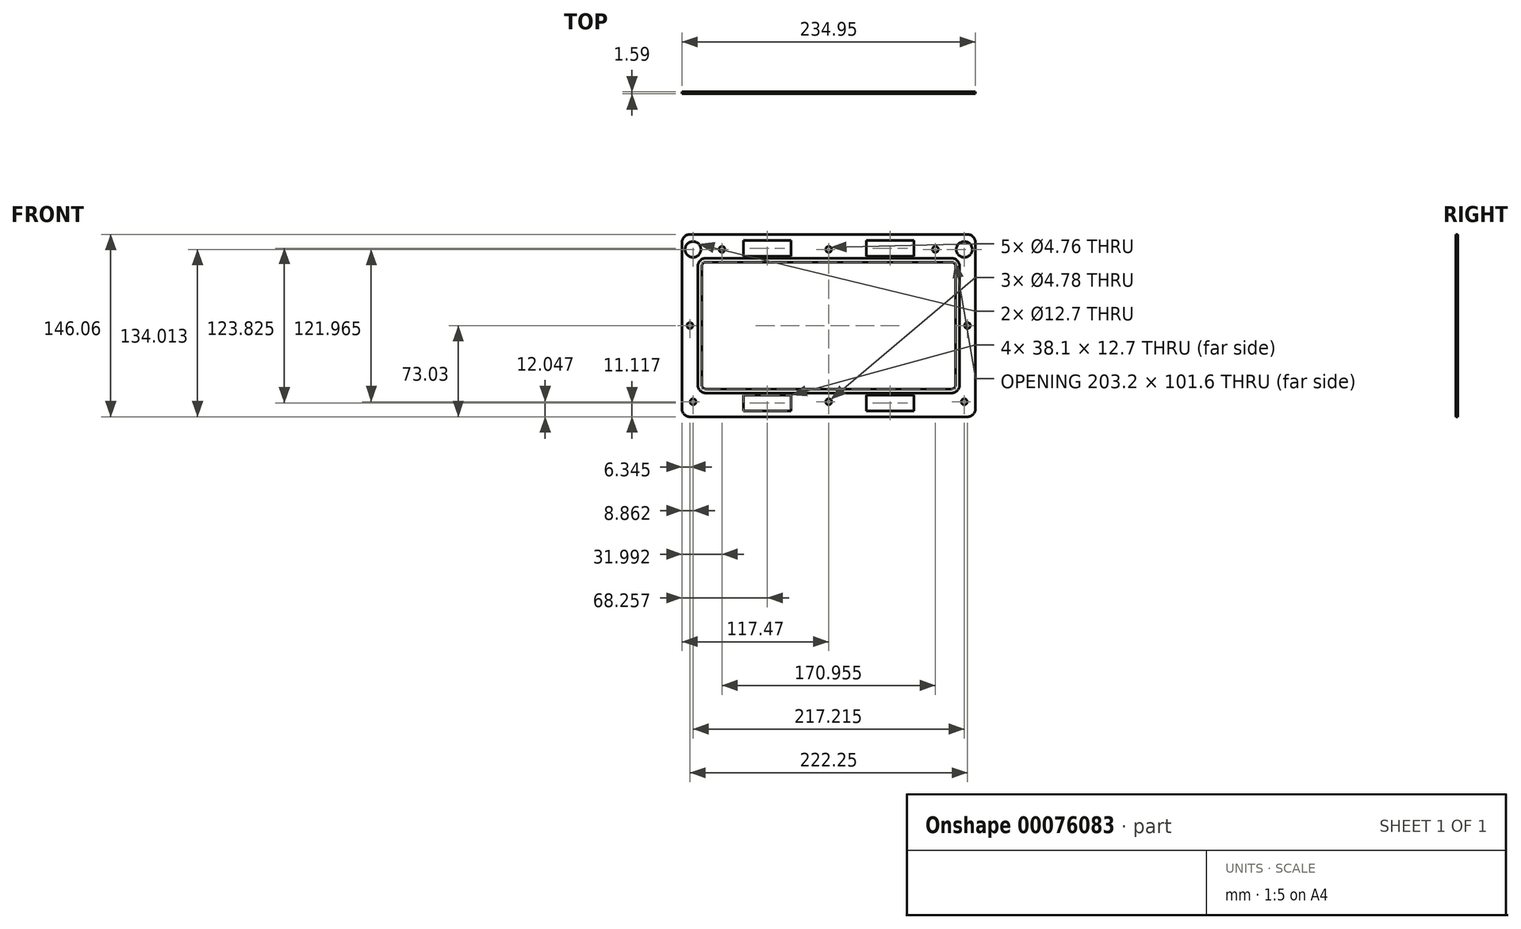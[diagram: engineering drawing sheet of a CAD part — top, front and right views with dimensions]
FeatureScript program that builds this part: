
annotation { "Feature Type Name" : "Feature", "Feature Type Description" : "" }
export const myFeature = defineFeature(function(context is Context, id is Id, definition is map)
    precondition{}
    {
        {
            var Q0;
            Q0=qCreatedBy(makeId("Front.planeOp"),FACE);
            var sketch = newSketch(context, id + "F0", { "sketchPlane" : qUnion([Q0])});
            skLineSegment(sketch, "E0.bottom", {"start": v(-98.43, 53.98) * mm, "end": v(98.43, 53.98) * mm});
            skLineSegment(sketch, "E0.top", {"start": v(-98.43, -53.97) * mm, "end": v(98.42, -53.97) * mm});
            skLineSegment(sketch, "E0.left", {"start": v(-104.78, 47.63) * mm, "end": v(-104.78, -47.62) * mm});
            skLineSegment(sketch, "E0.right", {"start": v(104.78, 47.63) * mm, "end": v(104.77, -47.62) * mm});
            skPoint(sketch, "E1.visualSharp", {"position": v(-104.78, 53.98) * mm});
            skArc(sketch, "E1.filletArc", {"start": v(-98.43, 53.98) * mm, "mid": v(-102.92, 52.12) * mm, "end": v(-104.78, 47.63) * mm});
            skPoint(sketch, "E2.visualSharp", {"position": v(104.78, 53.98) * mm});
            skArc(sketch, "E2.filletArc", {"start": v(104.78, 47.63) * mm, "mid": v(102.92, 52.12) * mm, "end": v(98.43, 53.98) * mm});
            skPoint(sketch, "E3.visualSharp", {"position": v(104.77, -53.97) * mm});
            skArc(sketch, "E3.filletArc", {"start": v(98.42, -53.97) * mm, "mid": v(102.92, -52.12) * mm, "end": v(104.77, -47.62) * mm});
            skPoint(sketch, "E4.visualSharp", {"position": v(-104.78, -53.97) * mm});
            skArc(sketch, "E4.filletArc", {"start": v(-104.78, -47.62) * mm, "mid": v(-102.92, -52.12) * mm, "end": v(-98.43, -53.97) * mm});
            skArc(sketch, "E5.0", {"start": v(-98.43, 50.8) * mm, "mid": v(-100.67, 49.87) * mm, "end": v(-101.6, 47.63) * mm});
            skLineSegment(sketch, "E5.1", {"start": v(-101.6, 47.63) * mm, "end": v(-101.6, -47.62) * mm});
            skLineSegment(sketch, "E5.2", {"start": v(-98.43, 50.8) * mm, "end": v(98.43, 50.8) * mm});
            skArc(sketch, "E5.3", {"start": v(-101.6, -47.62) * mm, "mid": v(-100.67, -49.87) * mm, "end": v(-98.43, -50.8) * mm});
            skArc(sketch, "E5.4", {"start": v(101.6, 47.63) * mm, "mid": v(100.67, 49.87) * mm, "end": v(98.43, 50.8) * mm});
            skLineSegment(sketch, "E5.5", {"start": v(101.6, 47.63) * mm, "end": v(101.6, -47.62) * mm});
            skArc(sketch, "E5.6", {"start": v(98.42, -50.8) * mm, "mid": v(100.67, -49.87) * mm, "end": v(101.6, -47.62) * mm});
            skLineSegment(sketch, "E5.7", {"start": v(-98.43, -50.8) * mm, "end": v(98.42, -50.8) * mm});
            skLineSegment(sketch, "E6.0", {"start": v(-111.12, 73.03) * mm, "end": v(111.13, 73.03) * mm});
            skLineSegment(sketch, "E7.0", {"start": v(-111.13, -73.02) * mm, "end": v(111.12, -73.02) * mm});
            skLineSegment(sketch, "E8.0", {"start": v(-117.47, 66.68) * mm, "end": v(-117.48, -66.67) * mm});
            skLineSegment(sketch, "E9.0", {"start": v(117.48, 66.68) * mm, "end": v(117.47, -66.67) * mm});
            skPoint(sketch, "E10.visualSharp", {"position": v(-117.47, 73.03) * mm});
            skArc(sketch, "E10.filletArc", {"start": v(-111.13, 73.03) * mm, "mid": v(-115.62, 71.17) * mm, "end": v(-117.47, 66.68) * mm});
            skPoint(sketch, "E11.visualSharp", {"position": v(117.48, 73.03) * mm});
            skArc(sketch, "E11.filletArc", {"start": v(117.47, 66.68) * mm, "mid": v(115.62, 71.17) * mm, "end": v(111.13, 73.03) * mm});
            skPoint(sketch, "E12.visualSharp", {"position": v(117.47, -73.02) * mm});
            skArc(sketch, "E12.filletArc", {"start": v(111.12, -73.02) * mm, "mid": v(115.62, -71.17) * mm, "end": v(117.47, -66.67) * mm});
            skPoint(sketch, "E13.visualSharp", {"position": v(-117.48, -73.02) * mm});
            skArc(sketch, "E13.filletArc", {"start": v(-117.48, -66.67) * mm, "mid": v(-115.62, -71.17) * mm, "end": v(-111.13, -73.02) * mm});
            skLineSegment(sketch, "E14", {"start": v(-117.48, 66.68) * mm, "end": v(-111.12, 73.03) * mm, "construction": true});
            skLineSegment(sketch, "E15", {"start": v(-114.3, 69.85) * mm, "end": v(-102.92, 52.12) * mm, "construction": true});
            skLineSegment(sketch, "E16", {"start": v(-117.48, 0) * mm, "end": v(-104.78, 0) * mm, "construction": true});
            skLineSegment(sketch, "E17", {"start": v(-111.13, -73.02) * mm, "end": v(-117.48, -66.67) * mm, "construction": true});
            skLineSegment(sketch, "E18", {"start": v(-114.3, -69.85) * mm, "end": v(-102.92, -52.12) * mm, "construction": true});
            skLineSegment(sketch, "E19", {"start": v(0, 94.31) * mm, "end": v(0, -140.3) * mm, "construction": true});
            skPoint(sketch, "E19.startSnap0", {"position": v(0, 73.03) * mm});
            skLineSegment(sketch, "E20", {"start": v(-149.8, 0) * mm, "end": v(205.48, 0) * mm, "construction": true});
            skLineSegment(sketch, "E21", {"start": v(-98.43, 53.98) * mm, "end": v(-98.43, 73.03) * mm, "construction": true});
            skCircle(sketch, "E22", {"center": v(-108.6, 60.98) * mm, "radius": 6.35 * mm});
            skCircle(sketch, "E23", {"center": v(-111.13, 0) * mm, "radius": 2.38 * mm});
            skCircle(sketch, "E24", {"center": v(-108.6, -60.98) * mm, "radius": 2.38 * mm});
            skLineSegment(sketch, "E25", {"start": v(-98.43, -53.97) * mm, "end": v(-98.43, -73.02) * mm, "construction": true});
            skLineSegment(sketch, "E26", {"start": v(-98.43, -73.02) * mm, "end": v(-98.43, -63.5) * mm, "construction": true});
            skLineSegment(sketch, "E27", {"start": v(0, 53.98) * mm, "end": v(0, 73.03) * mm, "construction": true});
            skLineSegment(sketch, "E28", {"start": v(0, -73.02) * mm, "end": v(0, -53.97) * mm, "construction": true});
            skCircle(sketch, "E29", {"center": v(0, 60.98) * mm, "radius": 2.38 * mm});
            skLineSegment(sketch, "E30.bottom", {"start": v(-30.16, 55.56) * mm, "end": v(-68.26, 55.56) * mm});
            skLineSegment(sketch, "E30.top", {"start": v(-30.16, 68.26) * mm, "end": v(-68.26, 68.26) * mm});
            skLineSegment(sketch, "E30.left", {"start": v(-30.16, 55.56) * mm, "end": v(-30.16, 68.26) * mm});
            skLineSegment(sketch, "E30.right", {"start": v(-68.26, 55.56) * mm, "end": v(-68.26, 68.26) * mm});
            skPoint(sketch, "E30.middle", {"position": v(-49.21, 61.91) * mm});
            skLineSegment(sketch, "E31.MirrorCS", {"start": v(30.16, 55.56) * mm, "end": v(30.16, 68.26) * mm});
            skLineSegment(sketch, "E32.MirrorCS", {"start": v(30.16, 68.26) * mm, "end": v(68.26, 68.26) * mm});
            skLineSegment(sketch, "E33.MirrorCS", {"start": v(68.26, 55.56) * mm, "end": v(68.26, 68.26) * mm});
            skLineSegment(sketch, "E34.MirrorCS", {"start": v(30.16, 55.56) * mm, "end": v(68.26, 55.56) * mm});
            skCircle(sketch, "E35.MirrorC", {"center": v(108.6, 60.98) * mm, "radius": 6.35 * mm});
            skCircle(sketch, "E36.MirrorC", {"center": v(111.13, 0) * mm, "radius": 2.38 * mm});
            skCircle(sketch, "E37.MirrorC", {"center": v(108.6, -60.98) * mm, "radius": 2.38 * mm});
            skLineSegment(sketch, "E38.MirrorCS", {"start": v(-68.26, -55.56) * mm, "end": v(-68.26, -68.26) * mm});
            skLineSegment(sketch, "E39.MirrorCS", {"start": v(-30.16, -55.56) * mm, "end": v(-30.16, -68.26) * mm});
            skLineSegment(sketch, "E40.MirrorCS", {"start": v(-30.16, -55.56) * mm, "end": v(-68.26, -55.56) * mm});
            skLineSegment(sketch, "E41.MirrorCS", {"start": v(-30.16, -68.26) * mm, "end": v(-68.26, -68.26) * mm});
            skLineSegment(sketch, "E42.MirrorCS", {"start": v(30.16, -55.56) * mm, "end": v(30.16, -68.26) * mm});
            skLineSegment(sketch, "E43.MirrorCS", {"start": v(30.16, -68.26) * mm, "end": v(68.26, -68.26) * mm});
            skLineSegment(sketch, "E44.MirrorCS", {"start": v(68.26, -55.56) * mm, "end": v(68.26, -68.26) * mm});
            skLineSegment(sketch, "E45.MirrorCS", {"start": v(30.16, -55.56) * mm, "end": v(68.26, -55.56) * mm});
            skLineSegment(sketch, "E46", {"start": v(49.21, 68.26) * mm, "end": v(49.21, 55.56) * mm, "construction": true});
            skLineSegment(sketch, "E47", {"start": v(-108.6, 60.98) * mm, "end": v(108.6, 60.98) * mm, "construction": true});
            skCircle(sketch, "E48", {"center": v(-85.48, 60.98) * mm, "radius": 2.39 * mm});
            skCircle(sketch, "E49", {"center": v(85.48, 60.98) * mm, "radius": 2.39 * mm});
            skLineSegment(sketch, "E50", {"start": v(-108.6, -60.98) * mm, "end": v(108.6, -60.98) * mm, "construction": true});
            skCircle(sketch, "E51", {"center": v(0, -60.98) * mm, "radius": 2.39 * mm});
            skSolve(sketch);
        }
        {
            var Q0;
            Q0 = qSketchRegion(id + "F0", true);
            var Q1;
            Q1=makeQuery(id+"F0.imprint","IMPRINT",FACE,{"disambiguationData":[TD([[makeQuery(id+"F0.imprint","IMPRINT",EDGE,{"derivedFrom":sQuery(id+"F0.wireOp",EDGE,"E0.bottom")}),-1.0]])]});
            extrude(context, id + "F1", {"entities" : qUnion([Q0, Q1]), "depth" : 0.8 * mm});
        }
        {
            var Q0;
            Q0 = qSketchRegion(id + "F0", true);
            extrude(context, id + "F2", {"entities" : qUnion([Q0]), "operationType" : NewBodyOperationType.ADD, "depth" : 1.59 * mm});
        }
    });
